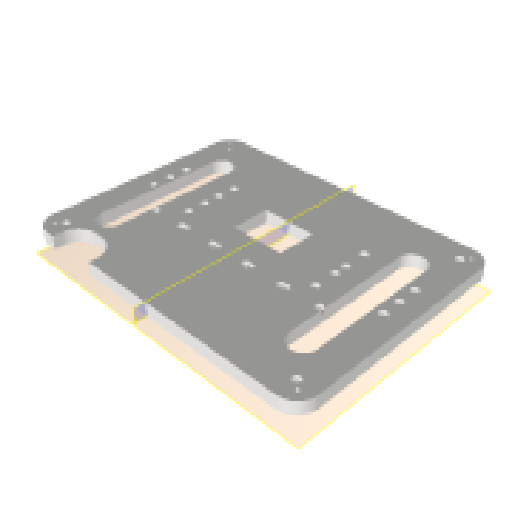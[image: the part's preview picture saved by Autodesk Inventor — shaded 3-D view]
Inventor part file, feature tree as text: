
AUTODESK INVENTOR PART (.ipt)
format: ipt  version: 2024.1 (Build 281209000, 209)  size: 351,744 bytes
history: native  units: mm
features: sketch x6, reference x6, other x5, projected_geometry x4, extrude x3, hole x3, plane x2, mirror x1
ambient origin geometry x8: Origin, YZ Plane, XZ Plane, XY Plane, X Axis, Y Axis, Z Axis, Center Point
bodies: Volumenkörper1 (feature_tree)
feature tree (30):
  plane  "Arbeitsebene1"
  extrude  "Extrusion1"  Depth=3.0mm
  hole  "Bohrung1"  [1 undecoded]
  extrude  "Extrusion3"  TaperAngle=0.0deg  [1 undecoded]
  hole  "Bohrung2"  [1 undecoded]
  plane  "Arbeitsebene2"
  mirror  "Spiegeln1"
  extrude  "Extrusion4"  Depth=3.5mm
  hole  "Bohrung3"  [1 undecoded]
  sketch  "Skizze1"  dims[d0=3.0mm d1=3.0mm]
  reference  "Referenz1"
  reference  "Referenz2"
  reference  "Referenz3"
  sketch  "Skizze3"  dims[d4=15.0mm d5=15.0mm]
  projected_geometry  "Projizierte Kontur2"
  sketch  "Skizze4"  dims[d6=10.0mm d7=-0.174533mm]
  reference  "Referenz4"
  reference  "Referenz5"
  sketch  "Skizze5"  dims[d10=2.8mm d11=6.0mm d12=6.5mm d13=3.5mm d14=90.0deg d15=8.0mm d16=20.594885mm d17=0.0mm d18=0.0mm]
  projected_geometry  "Projizierte Kontur3"
  reference  "Referenz6"
  sketch  "Skizze6"  dims[d19=50.0mm d21=30.0mm d22=10.0mm d24=10.0mm]
  projected_geometry  "Projizierte Kontur4"
  sketch  "Skizze7"  dims[d26=2.8mm d27=6.0mm d28=4.0mm d29=2.0mm d30=90.0deg d31=8.0mm d32=20.594885mm d34=20.0mm d36=15.0mm d37=20.0mm d39=15.0mm d42=1.5mm d43=1.5mm d44=50.0mm d45=20.0mm d46=20.0mm d47=0.0mm d48=0.0mm d49=2.8mm d50=6.0mm d51=6.5mm d52=3.5mm d53=90.0deg d54=8.0mm d55=150.0deg d56=5.0mm]
  projected_geometry  "Projizierte Kontur5"
  other  "Assembly_Planktoscope_Uc2version_wormdrive_V3.iam"
  other  "60_Planktoscope_RaspiScreenHolder_v0:1"
  other  "60_Planktoscope_Base_half_wormdrive_1:1"
  other  "60_Planktoscope_Base_half_wormdrive_1_MIR:1"
  other  "00_NEMA_17:1"
note: 4 required parameter values undecoded (feature->parameter linkage not recoverable at this tier; creation-order binding heuristic only, values carry confidence <= 0.55)
